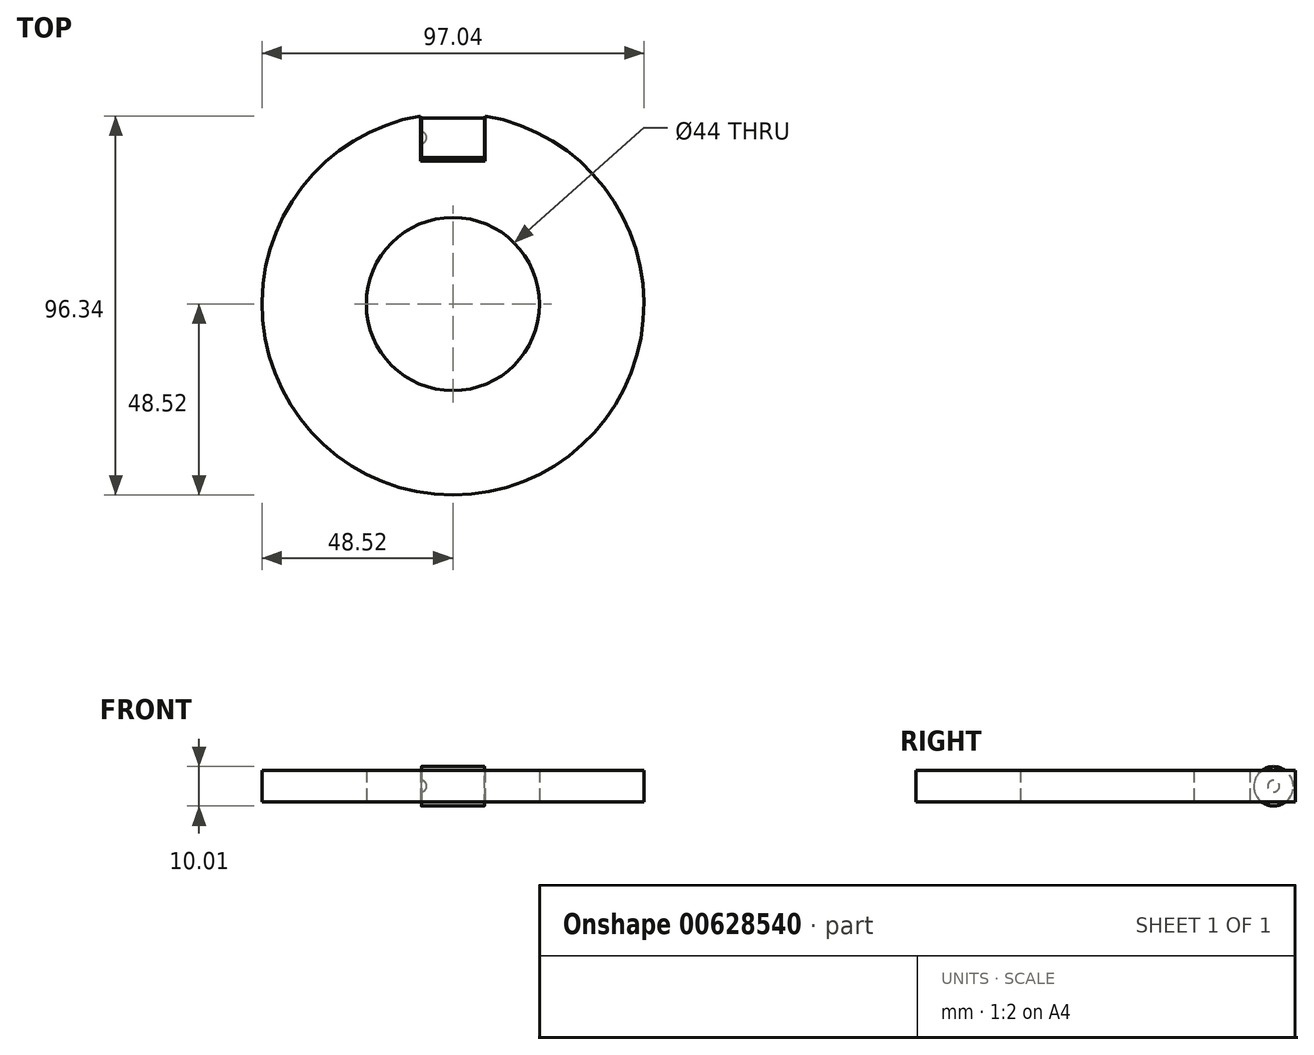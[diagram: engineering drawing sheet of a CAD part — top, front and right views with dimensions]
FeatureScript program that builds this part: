
annotation { "Feature Type Name" : "Feature", "Feature Type Description" : "" }
export const myFeature = defineFeature(function(context is Context, id is Id, definition is map)
    precondition{}
    {
        {
            var Q0;
            Q0=qCreatedBy(makeId("Top.planeOp"),FACE);
            var sketch = newSketch(context, id + "F0", { "sketchPlane" : qUnion([Q0])});
            skCircle(sketch, "E0", {"center": v(0, 0) * mm, "radius": 48.52 * mm});
            skCircle(sketch, "E1", {"center": v(0, 0) * mm, "radius": 22 * mm});
            skSolve(sketch);
        }
        {
            var Q0;
            Q0=makeQuery(id+"F0.imprint","IMPRINT",FACE,{"disambiguationData":[TD([[makeQuery(id+"F0.imprint","IMPRINT",EDGE,{"derivedFrom":sQuery(id+"F0.wireOp",EDGE,"E0")}),1.0]])]});
            extrude(context, id + "F1", {"entities" : qUnion([Q0]), "depth" : 8 * mm, "offsetDistance" : 25.4 * mm});
        }
        {
            var Q0;
            Q0=qCreatedBy(makeId("Top.planeOp"),FACE);
            var sketch = newSketch(context, id + "F2", { "sketchPlane" : qUnion([Q0])});
            skCircle(sketch, "E2.0.0", {"center": v(0, 0) * mm, "radius": 48.52 * mm, "construction": true});
            skLineSegment(sketch, "E3", {"start": v(-8.18, 47.82) * mm, "end": v(-8.18, 36.28) * mm});
            skLineSegment(sketch, "E4", {"start": v(-8.18, 36.28) * mm, "end": v(0, 36.28) * mm});
            skLineSegment(sketch, "E5", {"start": v(0, 36.28) * mm, "end": v(8.18, 36.28) * mm});
            skLineSegment(sketch, "E6", {"start": v(8.18, 36.28) * mm, "end": v(8.18, 54.08) * mm});
            skLineSegment(sketch, "E7", {"start": v(8.18, 54.08) * mm, "end": v(-8.18, 54.08) * mm});
            skLineSegment(sketch, "E8", {"start": v(-8.18, 54.08) * mm, "end": v(-8.18, 47.82) * mm});
            skSolve(sketch);
        }
        {
            var Q0;
            Q0 = qSketchRegion(id + "F2", true);
            extrude(context, id + "F3", {"entities" : qUnion([Q0]), "operationType" : NewBodyOperationType.REMOVE, "depth" : 25.4 * mm, "offsetDistance" : 25.4 * mm});
        }
        {
            var Q0;
            Q0=makeQuery(id+"F3.boolean.opBoolean","COPY",FACE,{"derivedFrom":makeQuery(id+"F3.opExtrude","SWEPT_FACE",FACE,{"disambiguationData":[OSD([sQuery(id+"F2.wireOp",EDGE,"E3"),sQuery(id+"F2.wireOp",EDGE,"E8")])]})});
            var sketch = newSketch(context, id + "F4", { "sketchPlane" : qUnion([Q0])});
            skLineSegment(sketch, "E9.0", {"start": v(36.28, 8) * mm, "end": v(47.82, 8) * mm});
            skLineSegment(sketch, "E10.0", {"start": v(47.82, 0) * mm, "end": v(47.82, 8) * mm});
            skLineSegment(sketch, "E11.0", {"start": v(36.28, 8) * mm, "end": v(36.28, 0) * mm});
            skLineSegment(sketch, "E12.0", {"start": v(47.82, 0) * mm, "end": v(36.28, 0) * mm});
            skCircle(sketch, "E13", {"center": v(43.48, 4) * mm, "radius": 1.72 * mm});
            skPoint(sketch, "E13.centerSnap0", {"position": v(36.28, 4) * mm});
            skPoint(sketch, "E13.centerSnap1", {"position": v(42.05, 0) * mm});
            skSolve(sketch);
        }
        {
            var Q0;
            Q0=makeQuery(id+"F3.boolean.opBoolean","COPY",FACE,{"derivedFrom":makeQuery(id+"F3.opExtrude","SWEPT_FACE",FACE,{"disambiguationData":[OSD([sQuery(id+"F2.wireOp",EDGE,"E4"),sQuery(id+"F2.wireOp",EDGE,"E5")])]})});
            cPlane(context, id + "F5", {"entities" : qUnion([Q0]), "cplaneType" : CPlaneType.OFFSET, "offset" : 6 * mm, "width" : 150 * mm, "height" : 150 * mm});
        }
        {
            var Q0;
            Q0=qCreatedBy(id+"F5.planeOp",FACE);
            var sketch = newSketch(context, id + "F6", { "sketchPlane" : qUnion([Q0])});
            skLineSegment(sketch, "E14.0", {"start": v(8.18, 0) * mm, "end": v(8.18, 8) * mm});
            skCircle(sketch, "E15", {"center": v(8.18, 4) * mm, "radius": 1.5 * mm});
            skCircle(sketch, "E16", {"center": v(8.18, 4) * mm, "radius": 1.8 * mm});
            skPoint(sketch, "E17.center.orphan", {"position": v(-8.18, 4) * mm});
            skPoint(sketch, "E18.trimOffspring.end.orphan", {"position": v(-8.18, 0) * mm});
            skPoint(sketch, "E19.0.start.orphan", {"position": v(-8.18, 8) * mm});
            skLineSegment(sketch, "E20", {"start": v(8.18, 4) * mm, "end": v(-2.21, 4) * mm, "construction": true});
            skLineSegment(sketch, "E21", {"start": v(6.38, 4) * mm, "end": v(8.18, 4) * mm});
            skSolve(sketch);
        }
        {
            var Q0;
            {var subQ0=sQuery(id+"F6.wireOp",EDGE,"E15");var subQ1=sQuery(id+"F6.wireOp",EDGE,"E14.0");var subQ2=makeQuery(id+"F6.imprint","INTERSECT",VERTEX,{"disambiguationData":[OD(0.0)],"derivedFrom":[subQ1,subQ0]});Q0=makeQuery(id+"F6.imprint","IMPRINT",FACE,{"disambiguationData":[TD([[makeQuery(id+"F6.imprint","IMPRINT",EDGE,{"disambiguationData":[TD([[subQ2,-1.0]])],"derivedFrom":subQ1}),1.0]])]});}
            var Q1;
            Q1=sQuery(id+"F6.wireOp",EDGE,"E20");
            revolve(context, id + "F7", {"operationType" : NewBodyOperationType.ADD, "entities" : qUnion([Q0]), "axis" : qUnion([Q1]), "revolveType" : RevolveType.FULL});
        }
        {
            var Q0;
            Q0=qCreatedBy(makeId("Right.planeOp"),FACE);
            var sketch = newSketch(context, id + "F8", { "sketchPlane" : qUnion([Q0])});
            skLineSegment(sketch, "E22.0.0", {"start": v(47.82, 0) * mm, "end": v(47.82, 8) * mm, "construction": true});
            skLineSegment(sketch, "E22.0.1", {"start": v(47.82, 8) * mm, "end": v(36.28, 8) * mm, "construction": true});
            skLineSegment(sketch, "E22.0.2", {"start": v(36.28, 8) * mm, "end": v(36.28, 0) * mm, "construction": true});
            skLineSegment(sketch, "E22.0.3", {"start": v(36.28, 0) * mm, "end": v(47.82, 0) * mm, "construction": true});
            skCircle(sketch, "E23.0", {"center": v(42.28, 4) * mm, "radius": 1.5 * mm, "construction": true});
            skCircle(sketch, "E24", {"center": v(42.28, 3.94) * mm, "radius": 5 * mm});
            skSolve(sketch);
        }
        {
            var Q0;
            Q0=makeQuery(id+"F8.imprint","IMPRINT",FACE,{"disambiguationData":[TD([[makeQuery(id+"F8.imprint","IMPRINT",EDGE,{"derivedFrom":sQuery(id+"F8.wireOp",EDGE,"E24")}),1.0]])]});
            extrude(context, id + "F9", {"entities" : qUnion([Q0]), "endBound" : BoundingType.SYMMETRIC, "depth" : 16 * mm, "offsetDistance" : 25 * mm});
        }
        {
            var Q0;
            {var subQ0=sQuery(id+"F6.wireOp",EDGE,"E16");var subQ1=sQuery(id+"F6.wireOp",EDGE,"E14.0");var subQ2=makeQuery(id+"F6.imprint","INTERSECT",VERTEX,{"disambiguationData":[OD(1.0)],"derivedFrom":[subQ1,subQ0]});Q0=makeQuery(id+"F6.imprint","IMPRINT",FACE,{"disambiguationData":[TD([[makeQuery(id+"F6.imprint","IMPRINT",EDGE,{"disambiguationData":[TD([[subQ2,1.0]])],"derivedFrom":subQ1}),1.0]])]});}
            var Q1;
            {var subQ0=sQuery(id+"F6.wireOp",EDGE,"E21");var subQ1=sQuery(id+"F6.wireOp",EDGE,"E14.0");var subQ2=makeQuery(id+"F6.imprint","INTERSECT",VERTEX,{"derivedFrom":[subQ1,subQ0]});Q1=makeQuery(id+"F6.imprint","IMPRINT",FACE,{"disambiguationData":[TD([[makeQuery(id+"F6.imprint","IMPRINT",EDGE,{"disambiguationData":[TD([[subQ2,-1.0]])],"derivedFrom":subQ1}),1.0]])]});}
            var Q2;
            Q2=sQuery(id+"F6.wireOp",EDGE,"E20");
            revolve(context, id + "F10", {"operationType" : NewBodyOperationType.REMOVE, "entities" : qUnion([Q0, Q1]), "axis" : qUnion([Q2]), "revolveType" : RevolveType.FULL});
        }
    });
